# Revit family: IS_ConnectAir_A7023_BIM_ES
name_source: partatom
category: Plumbing Fixtures
revit_build: Autodesk Revit 2017 (Build: 20160225_1515(x64)
units: mm (PartAtom-declared; Revit-internal decimal feet)

## family parameters
Always vertical = No
Cut with Voids When Loaded = No
OmniClass Number = 23.45.55.17
OmniClass Title = Mixing Faucets
Part Type = Normal
Room Calculation Point = No
Round Connector Dimension = Use Diameter
Shared = No
Work Plane-Based = No

## types (1)
- A7023AA - CONNECT AIR BSN MXR RMTD SLM HGH/SPT
    Acabado = Cromo
    Accesorios = https://www.idealstandard.es
    AlturaNominal = 85 mm  [stored 0.278871 ft]
    AnchuraNominal = 215 mm
    Autor = Ideal Standard Iberia
    Ayuda = https://www.idealstandard.es
    Cost = 0 $
    CódigoDeBarras = 4015413342001
    DescripciónUniclass2015 = Washbasin taps
    Description = CONNCT AIR BSN MXR RMTD SLM HGH/SPT
    Destacado = C.AIR M.LAV  CAÑO ALTO CHR 5L/M S/VAL
    Dimensiones = 85 x 345 x 215 mm
    DiámetroDeDesagüe = 0
    Espacio = Interno
    FechaDeCreación = 18/09/2020
    GarantíaDeLasPiezas = 2
    GarantíaPiezas = 2
    GrosorDelMaterial = 0
    GuíaDeInstallación = https://www.idealstandard.es
    IfcExportaComo = IfcValveType
    InformaciónDeProducto = https://www.idealstandard.es
    Installation instructions = https://www.idealstandard.es
    LongitudNominal = 345 mm  [stored 1.13189 ft]
    Maneta = No
    Manufacturer = https://www.idealstandard.es
    Marca = Ideal Standard Iberia
    Model = A7023AA
    NivelDeDesbordamiento = 0
    Nombre = Washbasintaps_ConnectAir_A7023_IdeaStandard
    NombreDeObjetoBim = IS_IdeaStandard_Washbasintaps_ConnectAir_A7023
    NúmeroDeModelo = A7023AA
    PesoBruto = 0
    PesoNeto = 2.33.
    PlatoDeDucha = No
    Product group = Washbasin manual water supply sets
    ProfundidadNominal = 345 mm  [stored 1.13189 ft]
    Referencia = A7023AA
    ReferenciaDeModelo = C.AIR M.LAV  CAÑO ALTO CHR 5L/M S/VAL
    ReferenciaUniclass2015 = Pr_40_20_87_98
    Repuestos = https://www.idealstandard.es
    Revisión = 1
    Teléfono = +34 93 561 80 00
    TipoDeConexión = Fontaneria
    TipoDeExportaciónIfc = MIXING
    TipoDeGarantía = Garantía del Fabricante
    URL = https://www.idealstandard.es
    Uniclass 2015 Code = Pr_40_20_87_96
    Uniclass 2015 Name = Washbasin manual water supply sets
    UnidadDeTiempo = año
    UnidadDeVolúmen = Litros
    UnidadDeÁrea = milímetros
    UnidadGarantía = año
    UnidadLineal = milímetros
    UnidadMonetaria = €
    UrlDelFabricante = https://www.idealstandard.es
    Versión = 1
    VersiónUniclass2015 = v1.1
    ÁreaDeMedición = Internal

note: [stored X ft] marks values corroborated as IEEE doubles in the binary element streams (Revit-internal decimal feet)

## geometry (parser evidence)
native form markers: Sweep x2
no freeform markers — native parametric forms only
